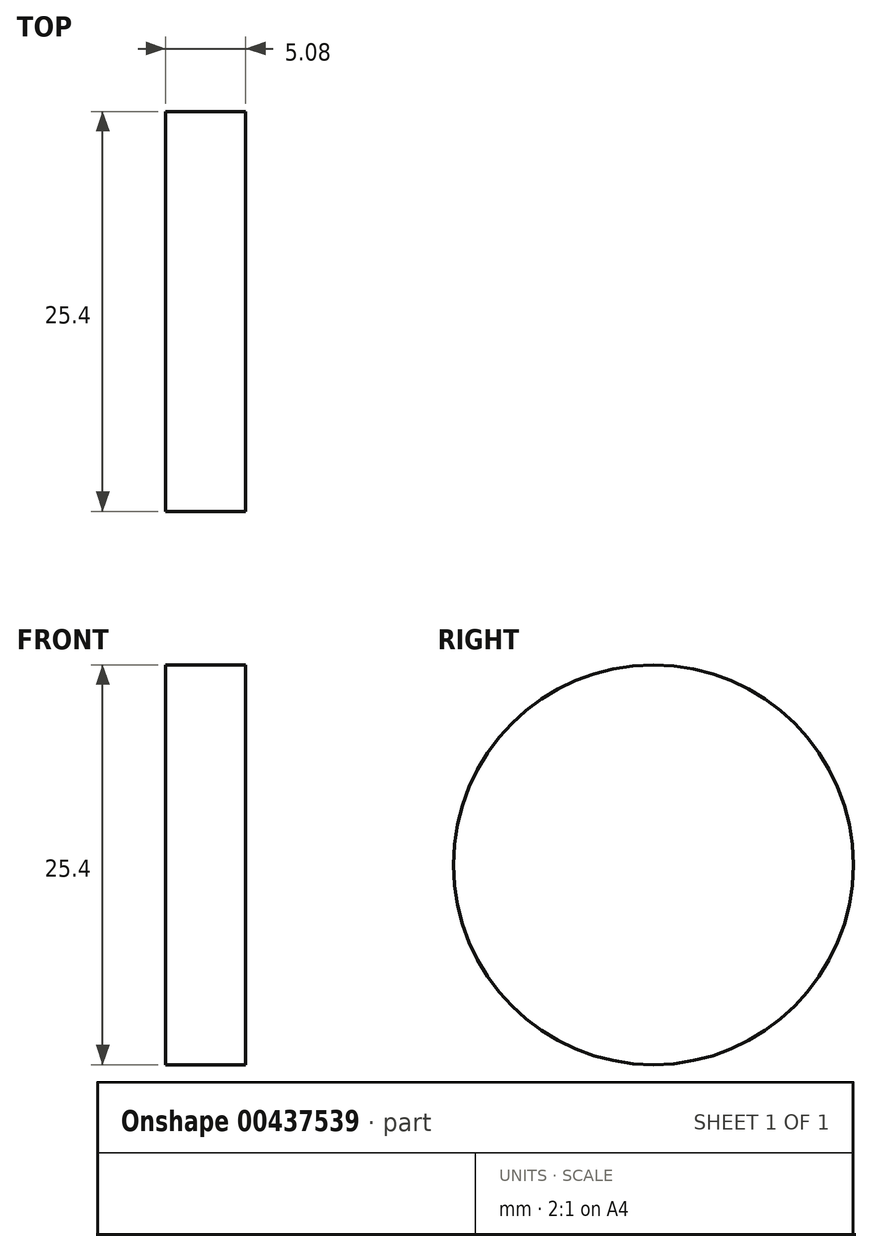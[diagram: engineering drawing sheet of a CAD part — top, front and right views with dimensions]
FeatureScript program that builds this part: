
annotation { "Feature Type Name" : "Feature", "Feature Type Description" : "" }
export const myFeature = defineFeature(function(context is Context, id is Id, definition is map)
    precondition{}
    {
        {
            var Q0;
            Q0=qCreatedBy(makeId("Right.planeOp"),FACE);
            var sketch = newSketch(context, id + "F0", { "sketchPlane" : qUnion([Q0])});
            skCircle(sketch, "E0", {"center": v(0, 0) * mm, "radius": 12.7 * mm});
            skSolve(sketch);
        }
        {
            var Q0;
            Q0 = qSketchRegion(id + "F0", true);
            extrude(context, id + "F1", {"entities" : qUnion([Q0]), "depth" : 5.08 * mm});
        }
    });
